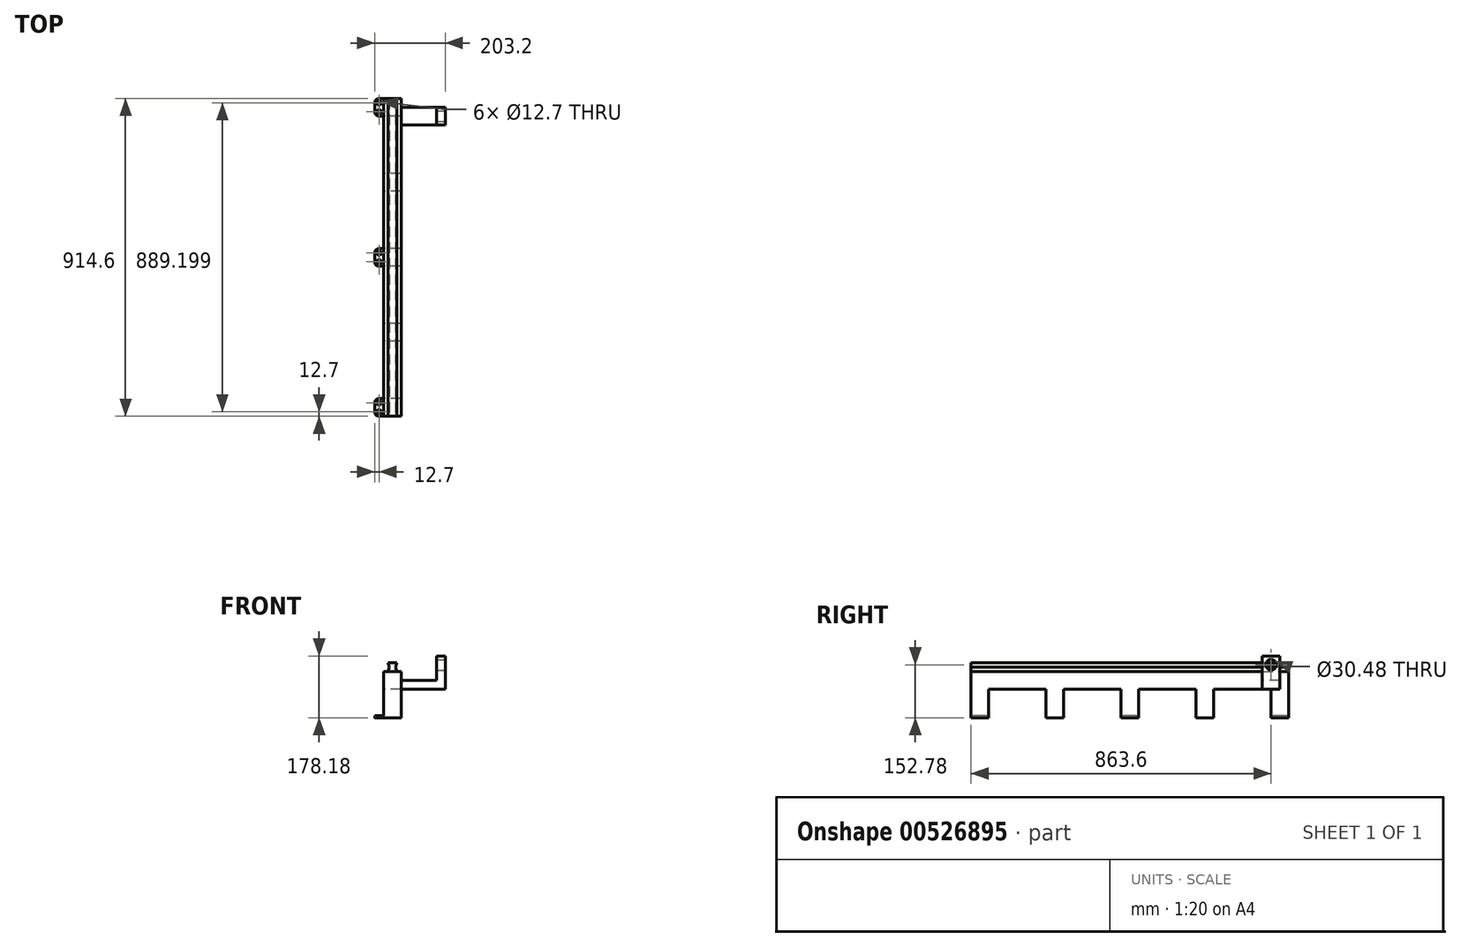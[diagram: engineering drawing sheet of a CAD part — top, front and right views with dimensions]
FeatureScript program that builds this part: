
annotation { "Feature Type Name" : "Feature", "Feature Type Description" : "" }
export const myFeature = defineFeature(function(context is Context, id is Id, definition is map)
    precondition{}
    {
        {
            var Q0;
            Q0=qCreatedBy(makeId("Right.planeOp"),FACE);
            var sketch = newSketch(context, id + "F0", { "sketchPlane" : qUnion([Q0])});
            skLineSegment(sketch, "E0", {"start": v(0, 0) * mm, "end": v(914.4, 0) * mm});
            skLineSegment(sketch, "E1", {"start": v(914.4, 0) * mm, "end": v(914.4, -133.73) * mm});
            skLineSegment(sketch, "E2", {"start": v(914.4, -133.73) * mm, "end": v(863.6, -133.73) * mm});
            skLineSegment(sketch, "E3", {"start": v(863.6, -50.8) * mm, "end": v(698.5, -50.8) * mm});
            skLineSegment(sketch, "E4", {"start": v(698.5, -50.8) * mm, "end": v(698.5, -133.73) * mm});
            skLineSegment(sketch, "E5", {"start": v(698.5, -133.73) * mm, "end": v(647.7, -133.73) * mm});
            skLineSegment(sketch, "E6", {"start": v(647.7, -50.8) * mm, "end": v(482.6, -50.8) * mm});
            skLineSegment(sketch, "E7", {"start": v(482.6, -50.8) * mm, "end": v(482.6, -133.73) * mm});
            skPoint(sketch, "E7.endSnap0", {"position": v(673.1, -133.73) * mm});
            skLineSegment(sketch, "E8", {"start": v(482.6, -133.73) * mm, "end": v(431.8, -133.73) * mm});
            skLineSegment(sketch, "E9", {"start": v(431.8, -133.73) * mm, "end": v(431.8, -50.8) * mm});
            skLineSegment(sketch, "E10", {"start": v(431.8, -50.8) * mm, "end": v(266.7, -50.8) * mm});
            skLineSegment(sketch, "E11", {"start": v(266.7, -50.8) * mm, "end": v(266.7, -133.73) * mm});
            skLineSegment(sketch, "E12", {"start": v(266.7, -133.73) * mm, "end": v(215.9, -133.73) * mm});
            skLineSegment(sketch, "E13", {"start": v(215.9, -50.8) * mm, "end": v(50.8, -50.8) * mm});
            skLineSegment(sketch, "E14", {"start": v(50.8, -50.8) * mm, "end": v(50.8, -133.73) * mm});
            skLineSegment(sketch, "E15", {"start": v(50.8, -133.73) * mm, "end": v(0, -133.73) * mm});
            skLineSegment(sketch, "E16", {"start": v(863.6, -50.8) * mm, "end": v(863.6, -133.73) * mm});
            skLineSegment(sketch, "E17", {"start": v(647.7, -133.73) * mm, "end": v(647.7, -50.8) * mm});
            skLineSegment(sketch, "E18", {"start": v(215.9, -50.8) * mm, "end": v(215.9, -133.73) * mm});
            skLineSegment(sketch, "E19", {"start": v(0, 0) * mm, "end": v(0, -133.73) * mm});
            skSolve(sketch);
        }
        {
            var Q0;
            Q0=makeQuery(id+"F0.imprint","IMPRINT",FACE,{"disambiguationData":[TD([[makeQuery(id+"F0.imprint","IMPRINT",EDGE,{"derivedFrom":sQuery(id+"F0.wireOp",EDGE,"E0")}),-1.0]])]});
            extrude(context, id + "F1", {"entities" : qUnion([Q0]), "depth" : 50.8 * mm, "offsetDistance" : 25.4 * mm});
        }
        {
            var Q0;
            Q0=qCreatedBy(makeId("Front.planeOp"),FACE);
            var sketch = newSketch(context, id + "F2", { "sketchPlane" : qUnion([Q0])});
            skLineSegment(sketch, "E20", {"start": v(0, 0) * mm, "end": v(12.7, 0) * mm});
            skLineSegment(sketch, "E21.bottom", {"start": v(12.7, 0) * mm, "end": v(38.1, 0) * mm});
            skLineSegment(sketch, "E22", {"start": v(12.7, 25.4) * mm, "end": v(38.1, 25.4) * mm});
            skLineSegment(sketch, "E23", {"start": v(12.7, 0) * mm, "end": v(16.63, 12.7) * mm});
            skLineSegment(sketch, "E24", {"start": v(16.63, 12.7) * mm, "end": v(12.7, 25.4) * mm});
            skLineSegment(sketch, "E25", {"start": v(25.4, 25.4) * mm, "end": v(25.4, 0) * mm, "construction": true});
            skLineSegment(sketch, "E26.MirrorCS", {"start": v(34.17, 12.7) * mm, "end": v(38.1, 25.4) * mm});
            skLineSegment(sketch, "E27.MirrorCS", {"start": v(38.1, 0) * mm, "end": v(34.17, 12.7) * mm});
            skSolve(sketch);
        }
        {
            var Q0;
            Q0=makeQuery(id+"F2.imprint","IMPRINT",FACE,{"disambiguationData":[TD([[makeQuery(id+"F2.imprint","IMPRINT",EDGE,{"derivedFrom":sQuery(id+"F2.wireOp",EDGE,"E21.bottom")}),1.0]])]});
            extrude(context, id + "F3", {"entities" : qUnion([Q0]), "oppositeDirection" : true, "depth" : 914.4 * mm, "offsetDistance" : 25.4 * mm});
        }
        {
            var Q0;
            Q0=qCreatedBy(makeId("Front.planeOp"),FACE);
            cPlane(context, id + "F4", {"entities" : qUnion([Q0]), "cplaneType" : CPlaneType.OFFSET, "offset" : 838.2 * mm, "oppositeDirection" : true, "width" : 152.4 * mm, "height" : 152.4 * mm});
        }
        {
            var Q0;
            Q0=qCreatedBy(id+"F4.planeOp",FACE);
            var sketch = newSketch(context, id + "F5", { "sketchPlane" : qUnion([Q0])});
            skLineSegment(sketch, "E28", {"start": v(0, -76.2) * mm, "end": v(0, -50.8) * mm});
            skLineSegment(sketch, "E29", {"start": v(152.4, -25.4) * mm, "end": v(0, -25.4) * mm});
            skLineSegment(sketch, "E30", {"start": v(177.8, -50.8) * mm, "end": v(0, -50.8) * mm});
            skLineSegment(sketch, "E31", {"start": v(152.4, -25.4) * mm, "end": v(152.4, 44.45) * mm});
            skLineSegment(sketch, "E32", {"start": v(177.8, -50.8) * mm, "end": v(177.8, 44.45) * mm});
            skLineSegment(sketch, "E33", {"start": v(177.8, 44.45) * mm, "end": v(152.4, 44.45) * mm});
            skLineSegment(sketch, "E34", {"start": v(0, -50.8) * mm, "end": v(0, -25.4) * mm});
            skSolve(sketch);
        }
        {
            var Q0;
            Q0 = qSketchRegion(id + "F5", true);
            extrude(context, id + "F6", {"entities" : qUnion([Q0]), "operationType" : NewBodyOperationType.ADD, "oppositeDirection" : true, "depth" : 50.8 * mm, "offsetDistance" : 25.4 * mm});
        }
        {
            var Q0;
            Q0=makeQuery(id+"F1.opExtrude","SWEPT_FACE",FACE,{"disambiguationData":[OSD([sQuery(id+"F0.wireOp",EDGE,"E15")])]});
            cPlane(context, id + "F7", {"entities" : qUnion([Q0]), "cplaneType" : CPlaneType.OFFSET, "offset" : 0 * mm, "width" : 152.4 * mm, "height" : 152.4 * mm});
        }
        {
            var Q0;
            Q0=qCreatedBy(id+"F7.planeOp",FACE);
            var sketch = newSketch(context, id + "F8", { "sketchPlane" : qUnion([Q0])});
            skLineSegment(sketch, "E35", {"start": v(0, 0) * mm, "end": v(0, -51.1) * mm});
            skLineSegment(sketch, "E36", {"start": v(0, -51.1) * mm, "end": v(-12.7, -51.1) * mm});
            skLineSegment(sketch, "E37", {"start": v(-25.4, -38.4) * mm, "end": v(-25.4, -12.7) * mm});
            skLineSegment(sketch, "E38", {"start": v(-12.7, 0) * mm, "end": v(0, 0) * mm});
            skPoint(sketch, "E39.visualSharp", {"position": v(-25.4, 0) * mm});
            skArc(sketch, "E39.filletArc", {"start": v(-12.7, 0) * mm, "mid": v(-21.68, -3.72) * mm, "end": v(-25.4, -12.7) * mm});
            skPoint(sketch, "E40.visualSharp", {"position": v(-25.4, -51.1) * mm});
            skArc(sketch, "E40.filletArc", {"start": v(-25.4, -38.4) * mm, "mid": v(-21.68, -47.38) * mm, "end": v(-12.7, -51.1) * mm});
            skCircle(sketch, "E41", {"center": v(-12.7, -38.4) * mm, "radius": 6.35 * mm});
            skCircle(sketch, "E42", {"center": v(-12.7, -12.7) * mm, "radius": 6.35 * mm});
            skLineSegment(sketch, "E43", {"start": v(0, -863.8) * mm, "end": v(0, -914.6) * mm});
            skLineSegment(sketch, "E44", {"start": v(0, -914.6) * mm, "end": v(-12.7, -914.6) * mm});
            skLineSegment(sketch, "E45", {"start": v(-25.4, -901.9) * mm, "end": v(-25.4, -876.5) * mm});
            skLineSegment(sketch, "E46", {"start": v(-12.7, -863.8) * mm, "end": v(0, -863.8) * mm});
            skPoint(sketch, "E47.visualSharp", {"position": v(-25.4, -863.8) * mm});
            skArc(sketch, "E47.filletArc", {"start": v(-12.7, -863.8) * mm, "mid": v(-21.68, -867.52) * mm, "end": v(-25.4, -876.5) * mm});
            skPoint(sketch, "E48.visualSharp", {"position": v(-25.4, -914.6) * mm});
            skArc(sketch, "E48.filletArc", {"start": v(-25.4, -901.9) * mm, "mid": v(-21.68, -910.88) * mm, "end": v(-12.7, -914.6) * mm});
            skCircle(sketch, "E49", {"center": v(-12.7, -876.5) * mm, "radius": 6.35 * mm});
            skCircle(sketch, "E50", {"center": v(-12.7, -901.9) * mm, "radius": 6.35 * mm});
            skLineSegment(sketch, "E51", {"start": v(0, -431.82) * mm, "end": v(0, -482.62) * mm});
            skLineSegment(sketch, "E52", {"start": v(0, -482.62) * mm, "end": v(-12.7, -482.62) * mm});
            skLineSegment(sketch, "E53", {"start": v(-25.4, -469.92) * mm, "end": v(-25.4, -444.52) * mm});
            skLineSegment(sketch, "E54", {"start": v(-12.7, -431.82) * mm, "end": v(0, -431.82) * mm});
            skPoint(sketch, "E55.visualSharp", {"position": v(-25.4, -431.82) * mm});
            skArc(sketch, "E55.filletArc", {"start": v(-12.7, -431.82) * mm, "mid": v(-21.68, -435.54) * mm, "end": v(-25.4, -444.52) * mm});
            skPoint(sketch, "E56.visualSharp", {"position": v(-25.4, -482.62) * mm});
            skArc(sketch, "E56.filletArc", {"start": v(-25.4, -469.92) * mm, "mid": v(-21.68, -478.9) * mm, "end": v(-12.7, -482.62) * mm});
            skCircle(sketch, "E57", {"center": v(-12.7, -444.52) * mm, "radius": 6.35 * mm});
            skCircle(sketch, "E58", {"center": v(-12.7, -469.92) * mm, "radius": 6.35 * mm});
            skSolve(sketch);
        }
        {
            var Q0;
            Q0 = qSketchRegion(id + "F8", true);
            extrude(context, id + "F9", {"entities" : qUnion([Q0]), "operationType" : NewBodyOperationType.ADD, "oppositeDirection" : true, "depth" : 6.35 * mm, "offsetDistance" : 25.4 * mm});
        }
        {
            var Q0;
            Q0=makeQuery(id+"F6.opExtrude","SWEPT_FACE",FACE,{"disambiguationData":[OSD([sQuery(id+"F5.wireOp",EDGE,"E32")])]});
            cPlane(context, id + "F10", {"entities" : qUnion([Q0]), "cplaneType" : CPlaneType.OFFSET, "offset" : 0 * mm, "width" : 152.4 * mm, "height" : 152.4 * mm});
        }
        {
            var Q0;
            Q0=qCreatedBy(id+"F10.planeOp",FACE);
            var sketch = newSketch(context, id + "F11", { "sketchPlane" : qUnion([Q0])});
            skCircle(sketch, "E59", {"center": v(863.6, 19.05) * mm, "radius": 15.24 * mm});
            skSolve(sketch);
        }
        {
            var Q0;
            Q0 = qSketchRegion(id + "F11", true);
            extrude(context, id + "F12", {"entities" : qUnion([Q0]), "operationType" : NewBodyOperationType.REMOVE, "oppositeDirection" : true, "depth" : 25.4 * mm, "offsetDistance" : 25.4 * mm});
        }
    });
